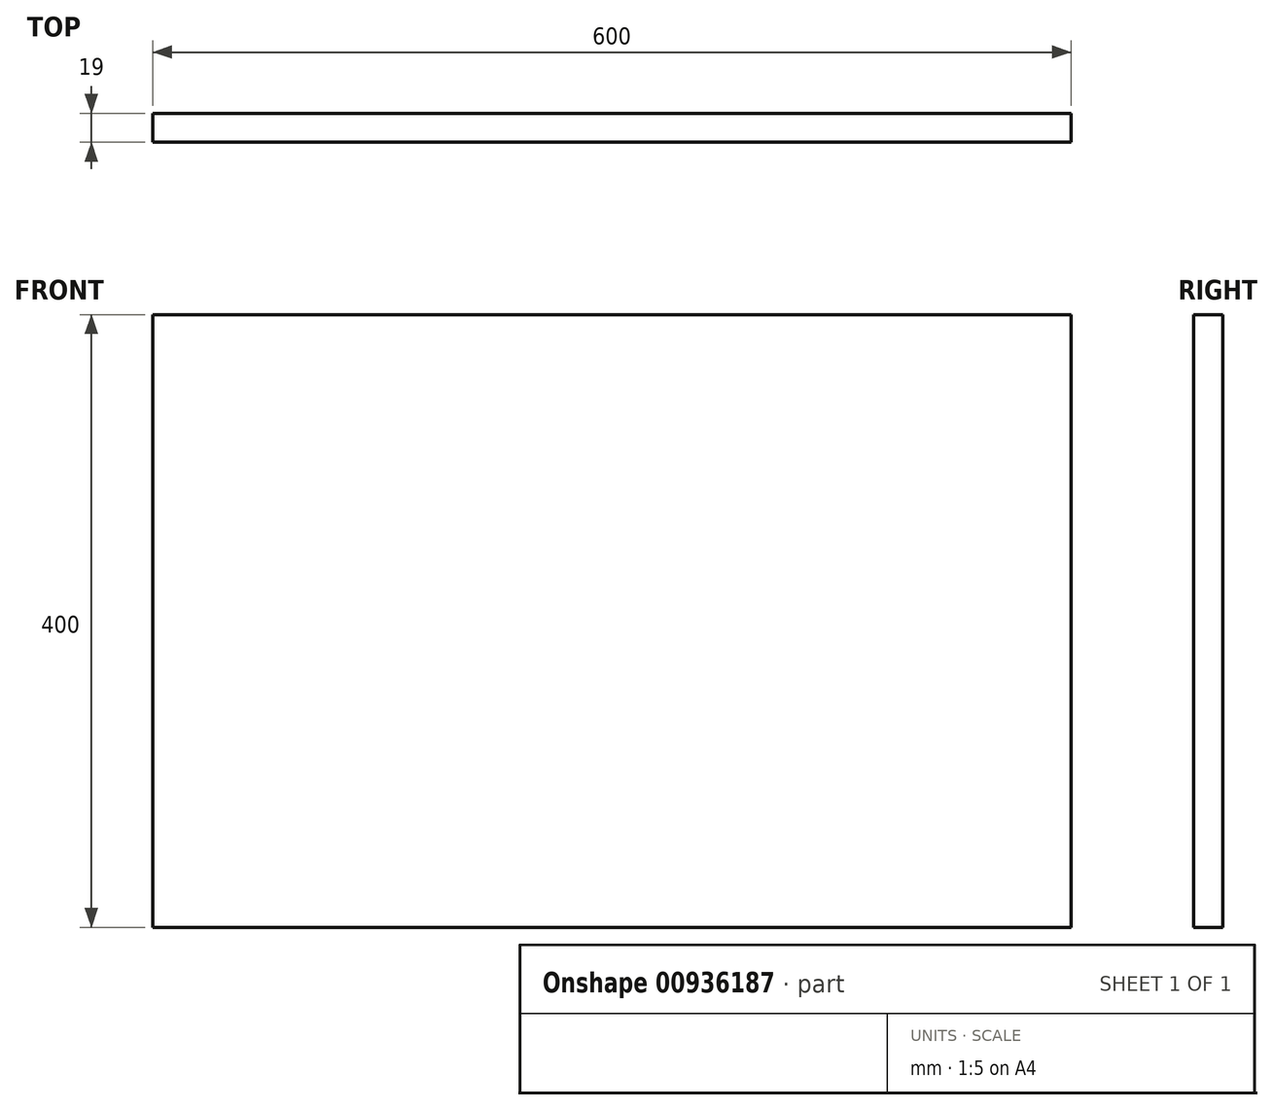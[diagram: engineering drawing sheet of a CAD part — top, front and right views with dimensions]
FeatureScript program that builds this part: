
annotation { "Feature Type Name" : "Feature", "Feature Type Description" : "" }
export const myFeature = defineFeature(function(context is Context, id is Id, definition is map)
    precondition{}
    {
        {
            var Q0;
            Q0=qCreatedBy(makeId("Front.planeOp"),FACE);
            var sketch = newSketch(context, id + "F0", { "sketchPlane" : qUnion([Q0])});
            skLineSegment(sketch, "E0.bottom", {"start": v(0, 0) * mm, "end": v(600, 0) * mm});
            skLineSegment(sketch, "E0.top", {"start": v(0, 400) * mm, "end": v(600, 400) * mm});
            skLineSegment(sketch, "E0.left", {"start": v(0, 0) * mm, "end": v(0, 400) * mm});
            skLineSegment(sketch, "E0.right", {"start": v(600, 0) * mm, "end": v(600, 400) * mm});
            skSolve(sketch);
        }
        {
            var Q0;
            Q0=qSketchRegion(id+"F0",true);
            extrude(context, id + "F1", {"entities" : qUnion([Q0]), "depth" : 19 * mm, "offsetDistance" : 25 * mm});
        }
    });
